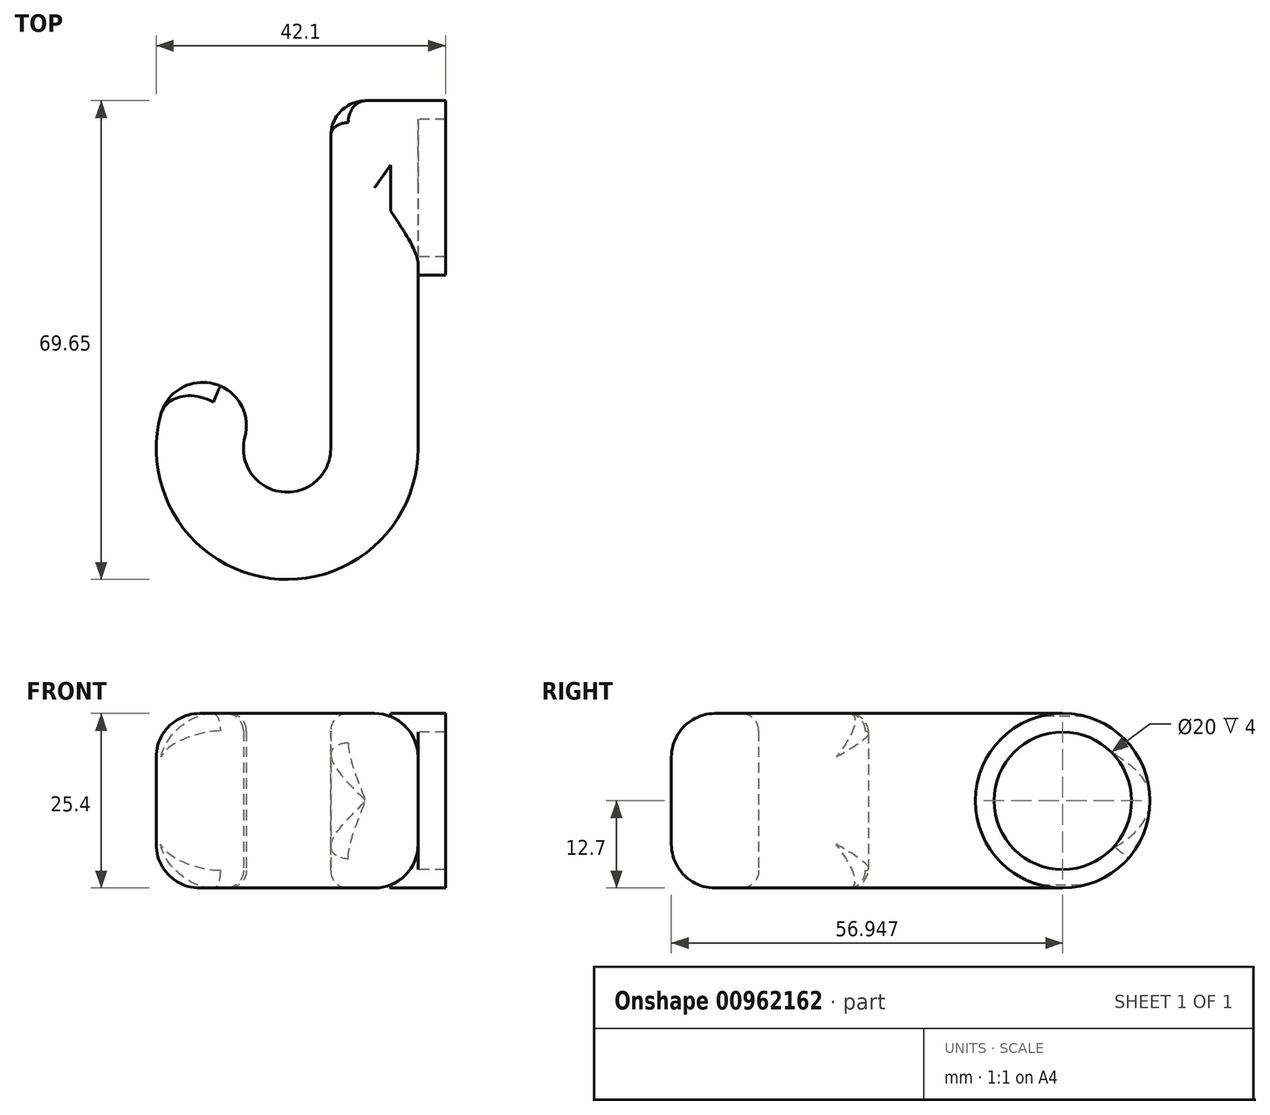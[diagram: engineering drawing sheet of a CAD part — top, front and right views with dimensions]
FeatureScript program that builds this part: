
annotation { "Feature Type Name" : "Feature", "Feature Type Description" : "" }
export const myFeature = defineFeature(function(context is Context, id is Id, definition is map)
    precondition{}
    {
        {
            var Q0;
            Q0=qCreatedBy(makeId("Top.planeOp"),FACE);
            var sketch = newSketch(context, id + "F0", { "sketchPlane" : qUnion([Q0])});
            skLineSegment(sketch, "E0", {"start": v(0, 38.1) * mm, "end": v(0, 12.7) * mm});
            skArc(sketch, "E1", {"start": v(10.84, 33.6) * mm, "mid": v(8.78, 43.97) * mm, "end": v(0, 38.1) * mm});
            skArc(sketch, "E2.0", {"start": v(19.82, 24.63) * mm, "mid": v(13.64, 55.7) * mm, "end": v(-12.7, 38.1) * mm});
            skLineSegment(sketch, "E3", {"start": v(10.84, 33.6) * mm, "end": v(19.82, 24.63) * mm});
            skArc(sketch, "E4", {"start": v(-23.54, 17.2) * mm, "mid": v(-21.48, 6.83) * mm, "end": v(-12.7, 12.7) * mm});
            skArc(sketch, "E5.0", {"start": v(-32.52, 26.17) * mm, "mid": v(-26.34, -4.9) * mm, "end": v(0, 12.7) * mm});
            skPoint(sketch, "E6.end.orphan", {"position": v(-19.05, 0) * mm});
            skPoint(sketch, "E7.orphan", {"position": v(-12.7, 12.7) * mm});
            skLineSegment(sketch, "E8", {"start": v(-23.54, 17.2) * mm, "end": v(-32.52, 26.17) * mm});
            skLineSegment(sketch, "E9", {"start": v(-12.7, 38.1) * mm, "end": v(-12.7, 12.7) * mm});
            skSolve(sketch);
        }
        {
            var Q0;
            Q0=qSketchRegion(id+"F0",true);
            extrude(context, id + "F1", {"entities" : qUnion([Q0]), "depth" : 76.2 * mm, "offsetDistance" : 25.4 * mm});
        }
        {
            var Q0;
            Q0=makeQuery(id+"F1.opExtrude","SWEPT_FACE",FACE,{"disambiguationData":[OSD([sQuery(id+"F0.wireOp",EDGE,"E9")])]});
            var sketch = newSketch(context, id + "F2", { "sketchPlane" : qUnion([Q0])});
            skLineSegment(sketch, "E10", {"start": v(0, 0) * mm, "end": v(-38.1, 0) * mm});
            skLineSegment(sketch, "E11", {"start": v(0, 76.2) * mm, "end": v(-38.1, 76.2) * mm});
            skLineSegment(sketch, "E12.bottom", {"start": v(-38.1, 0) * mm, "end": v(-25.4, 0) * mm});
            skLineSegment(sketch, "E12.top", {"start": v(-38.1, 76.2) * mm, "end": v(-25.4, 76.2) * mm});
            skLineSegment(sketch, "E12.right", {"start": v(-25.4, 0) * mm, "end": v(-25.4, 25.4) * mm});
            skLineSegment(sketch, "E13", {"start": v(-38.1, 50.8) * mm, "end": v(-57.15, 50.8) * mm});
            skLineSegment(sketch, "E14.MirrorCS", {"start": v(-38.1, 25.4) * mm, "end": v(-57.15, 25.4) * mm});
            skLineSegment(sketch, "E15", {"start": v(-57.15, 25.4) * mm, "end": v(-57.15, 50.8) * mm});
            skLineSegment(sketch, "E16.bottom", {"start": v(-25.4, 0) * mm, "end": v(6.35, 0) * mm});
            skLineSegment(sketch, "E16.top", {"start": v(-25.4, 25.4) * mm, "end": v(6.35, 25.4) * mm});
            skLineSegment(sketch, "E16.right", {"start": v(6.35, 0) * mm, "end": v(6.35, 25.4) * mm});
            skLineSegment(sketch, "E17", {"start": v(-25.4, 50.8) * mm, "end": v(6.35, 50.8) * mm});
            skLineSegment(sketch, "E18", {"start": v(6.35, 50.8) * mm, "end": v(6.35, 76.2) * mm});
            skLineSegment(sketch, "E19", {"start": v(6.35, 76.2) * mm, "end": v(-25.4, 76.2) * mm});
            skPoint(sketch, "E20.end.orphan", {"position": v(-25.4, 38.1) * mm});
            skPoint(sketch, "E20.start.orphan", {"position": v(-38.1, 38.1) * mm});
            skLineSegment(sketch, "E21", {"start": v(-38.1, 0) * mm, "end": v(-38.1, 76.2) * mm});
            skPoint(sketch, "E22.orphan", {"position": v(-25.4, 25.4) * mm});
            skLineSegment(sketch, "E23.trimOffspring", {"start": v(-25.4, 50.8) * mm, "end": v(-25.4, 76.2) * mm});
            skSolve(sketch);
        }
        {
            var Q0;
            {var subQ0=sQuery(id+"F2.wireOp",EDGE,"E13");Q0=makeQuery(id+"F2.imprint","IMPRINT",FACE,{"disambiguationData":[TD([[makeQuery(id+"F2.imprint","IMPRINT",EDGE,{"derivedFrom":subQ0}),1.0]])]});}
            extrude(context, id + "F3", {"entities" : qUnion([Q0]), "operationType" : NewBodyOperationType.REMOVE, "endBound" : BoundingType.THROUGH_ALL, "oppositeDirection" : true, "depth" : 25.4 * mm, "offsetDistance" : 25.4 * mm});
        }
        {
            var Q0;
            Q0=qSketchRegion(id+"F2",true);
            extrude(context, id + "F4", {"entities" : qUnion([Q0]), "operationType" : NewBodyOperationType.REMOVE, "oppositeDirection" : true, "depth" : 25.4 * mm, "offsetDistance" : 25.4 * mm});
        }
        {
            var Q0;
            Q0=makeQuery(id+"F3.boolean.opBoolean","COPY",FACE,{"disambiguationData":[TD([makeQuery(id+"F1.opExtrude","SWEPT_FACE",FACE,{"disambiguationData":[OSD([sQuery(id+"F0.wireOp",EDGE,"E1")])]}),makeQuery(id+"F1.opExtrude","SWEPT_FACE",FACE,{"disambiguationData":[OSD([sQuery(id+"F0.wireOp",EDGE,"E2.0")])]}),makeQuery(id+"F3.opExtrude","SWEPT_FACE",FACE,{"disambiguationData":[OSD([sQuery(id+"F2.wireOp",EDGE,"E13")])]}),makeQuery(id+"F3.opExtrude","SWEPT_FACE",FACE,{"disambiguationData":[OSD([sQuery(id+"F2.wireOp",EDGE,"E14.MirrorCS")])]})])],"derivedFrom":makeQuery(id+"F3.opExtrude","SWEPT_FACE",FACE,{"disambiguationData":[OSD([sQuery(id+"F2.wireOp",EDGE,"E21")])]})});
            var sketch = newSketch(context, id + "F5", { "sketchPlane" : qUnion([Q0])});
            skLineSegment(sketch, "E24.bottom", {"start": v(-25.4, 50.8) * mm, "end": v(-9.42, 50.8) * mm});
            skLineSegment(sketch, "E24.top", {"start": v(-25.4, 25.4) * mm, "end": v(-9.42, 25.4) * mm});
            skLineSegment(sketch, "E24.left", {"start": v(-25.4, 50.8) * mm, "end": v(-25.4, 25.4) * mm});
            skLineSegment(sketch, "E24.right", {"start": v(-9.42, 50.8) * mm, "end": v(-9.42, 25.4) * mm});
            skSolve(sketch);
        }
        {
            var Q0;
            Q0=qSketchRegion(id+"F5",true);
            extrude(context, id + "F6", {"entities" : qUnion([Q0]), "operationType" : NewBodyOperationType.REMOVE, "endBound" : BoundingType.THROUGH_ALL, "oppositeDirection" : true, "depth" : 25.4 * mm, "offsetDistance" : 25.4 * mm});
        }
        {
            var Q0;
            Q0=makeQuery(id+"F4.boolean.opBoolean","COPY",FACE,{"derivedFrom":makeQuery(id+"F4.opExtrude","CAP_FACE",FACE,{"disambiguationData":[OSD([sQuery(id+"F2.wireOp",EDGE,"E17"),sQuery(id+"F2.wireOp",EDGE,"E18"),sQuery(id+"F2.wireOp",EDGE,"E19"),sQuery(id+"F2.wireOp",EDGE,"E23.trimOffspring")])],"isStart":true})});
            var sketch = newSketch(context, id + "F7", { "sketchPlane" : qUnion([Q0])});
            skLineSegment(sketch, "E25.bottom", {"start": v(17.29, 76.2) * mm, "end": v(-6.4, 76.2) * mm});
            skLineSegment(sketch, "E25.top", {"start": v(17.29, 50.8) * mm, "end": v(-6.4, 50.8) * mm});
            skLineSegment(sketch, "E25.left", {"start": v(17.29, 76.2) * mm, "end": v(17.29, 50.8) * mm});
            skLineSegment(sketch, "E25.right", {"start": v(-6.4, 76.2) * mm, "end": v(-6.4, 50.8) * mm});
            skLineSegment(sketch, "E26.MirrorCS", {"start": v(17.29, 0) * mm, "end": v(17.29, 25.4) * mm});
            skLineSegment(sketch, "E27.MirrorCS", {"start": v(17.29, 25.4) * mm, "end": v(-6.4, 25.4) * mm});
            skLineSegment(sketch, "E28.MirrorCS", {"start": v(-6.4, 0) * mm, "end": v(-6.4, 25.4) * mm});
            skLineSegment(sketch, "E29.MirrorCS", {"start": v(17.29, 0) * mm, "end": v(-6.4, 0) * mm});
            skSolve(sketch);
        }
        {
            var Q0;
            Q0=qSketchRegion(id+"F7",true);
            extrude(context, id + "F8", {"entities" : qUnion([Q0]), "operationType" : NewBodyOperationType.REMOVE, "endBound" : BoundingType.THROUGH_ALL, "oppositeDirection" : true, "depth" : 25.4 * mm, "offsetDistance" : 25.4 * mm});
        }
        {
            var Q0;
            Q0=makeQuery(id+"F8.boolean.opBoolean","COPY",FACE,{"derivedFrom":makeQuery(id+"F8.opExtrude","SWEPT_FACE",FACE,{"disambiguationData":[OSD([sQuery(id+"F7.wireOp",EDGE,"E25.left")])]})});
            var sketch = newSketch(context, id + "F9", { "sketchPlane" : qUnion([Q0])});
            skLineSegment(sketch, "E30", {"start": v(-37.54, 76.2) * mm, "end": v(-37.54, 50.8) * mm});
            skLineSegment(sketch, "E31", {"start": v(-37.54, 50.8) * mm, "end": v(-23.64, 50.8) * mm});
            skLineSegment(sketch, "E32", {"start": v(-23.64, 50.8) * mm, "end": v(-23.64, 76.2) * mm});
            skLineSegment(sketch, "E33", {"start": v(-23.64, 76.2) * mm, "end": v(-37.54, 76.2) * mm});
            skLineSegment(sketch, "E34.MirrorCS", {"start": v(-37.54, 25.4) * mm, "end": v(-23.64, 25.4) * mm});
            skLineSegment(sketch, "E35.MirrorCS", {"start": v(-37.54, 0) * mm, "end": v(-37.54, 25.4) * mm});
            skLineSegment(sketch, "E36.MirrorCS", {"start": v(-23.64, 25.4) * mm, "end": v(-23.64, 0) * mm});
            skLineSegment(sketch, "E37.MirrorCS", {"start": v(-23.64, 0) * mm, "end": v(-37.54, 0) * mm});
            skSolve(sketch);
        }
        {
            var Q0;
            Q0=qSketchRegion(id+"F9",true);
            extrude(context, id + "F10", {"entities" : qUnion([Q0]), "operationType" : NewBodyOperationType.REMOVE, "endBound" : BoundingType.THROUGH_ALL, "oppositeDirection" : true, "depth" : 25.4 * mm, "offsetDistance" : 25.4 * mm});
        }
        {
            var Q0;
            Q0=makeQuery(id+"F4.boolean.opBoolean","INTERSECT",EDGE,{"derivedFrom":[makeQuery(id+"F1.opExtrude","SWEPT_FACE",FACE,{"disambiguationData":[OSD([sQuery(id+"F0.wireOp",EDGE,"E0")])]}),makeQuery(id+"F4.opExtrude","SWEPT_FACE",FACE,{"disambiguationData":[OSD([sQuery(id+"F2.wireOp",EDGE,"E12.right")])]})]});
            var Q1;
            Q1=makeQuery(id+"F4.boolean.opBoolean","COPY",EDGE,{"derivedFrom":makeQuery(id+"F4.opExtrude","CAP_EDGE",EDGE,{"disambiguationData":[OSD([sQuery(id+"F2.wireOp",EDGE,"E12.right")])],"isStart":true})});
            var Q2;
            Q2=makeQuery(id+"F4.boolean.opBoolean","INTERSECT",EDGE,{"derivedFrom":[makeQuery(id+"F1.opExtrude","SWEPT_FACE",FACE,{"disambiguationData":[OSD([sQuery(id+"F0.wireOp",EDGE,"E0")])]}),makeQuery(id+"F4.opExtrude","SWEPT_FACE",FACE,{"disambiguationData":[OSD([sQuery(id+"F2.wireOp",EDGE,"E23.trimOffspring")])]})]});
            var Q3;
            Q3=makeQuery(id+"F4.boolean.opBoolean","COPY",EDGE,{"derivedFrom":makeQuery(id+"F4.opExtrude","CAP_EDGE",EDGE,{"disambiguationData":[OSD([sQuery(id+"F2.wireOp",EDGE,"E23.trimOffspring")])],"isStart":true})});
            var Q4;
            {var subQ0=sQuery(id+"F0.wireOp",EDGE,"E0");Q4=makeQuery(id+"F3.boolean.opBoolean","SPLIT",EDGE,{"disambiguationData":[topologyDisambiguationEdgeConnected([makeQuery(id+"F1.opExtrude","SWEPT_FACE",FACE,{"disambiguationData":[OSD([subQ0])]}),makeQuery(id+"F3.opExtrude","SWEPT_FACE",FACE,{"disambiguationData":[OSD([sQuery(id+"F2.wireOp",EDGE,"E21")])]})])],"derivedFrom":makeQuery(id+"F1.opExtrude","SWEPT_EDGE",EDGE,{"disambiguationData":[OSD([subQ0,sQuery(id+"F0.wireOp",EDGE,"E1")])]})});}
            var Q5;
            Q5=makeQuery(id+"F3.boolean.opBoolean","MERGE",EDGE,{"derivedFrom":[makeQuery(id+"F1.opExtrude","SWEPT_EDGE",EDGE,{"disambiguationData":[OSD([sQuery(id+"F0.wireOp",EDGE,"E2.0"),sQuery(id+"F0.wireOp",EDGE,"E9")])]})],"fromTools":[makeQuery(id+"F3.opExtrude","CAP_EDGE",EDGE,{"disambiguationData":[OSD([sQuery(id+"F2.wireOp",EDGE,"E21")])],"isStart":true})]});
            var Q6;
            {var subQ0=sQuery(id+"F0.wireOp",EDGE,"E3");var subQ1=sQuery(id+"F0.wireOp",EDGE,"E2.0");Q6=makeQuery(id+"F6.boolean.opBoolean","SPLIT",EDGE,{"disambiguationData":[TD([makeQuery(id+"F3.boolean.opBoolean","COPY",FACE,{"derivedFrom":makeQuery(id+"F3.opExtrude","SWEPT_FACE",FACE,{"disambiguationData":[OSD([sQuery(id+"F2.wireOp",EDGE,"E14.MirrorCS")])]})})])],"derivedFrom":makeQuery(id+"F1.opExtrude","SWEPT_EDGE",EDGE,{"disambiguationData":[OSD([subQ1,subQ0])]})});}
            var Q7;
            {var subQ0=sQuery(id+"F0.wireOp",EDGE,"E3");var subQ1=sQuery(id+"F0.wireOp",EDGE,"E1");Q7=makeQuery(id+"F6.boolean.opBoolean","SPLIT",EDGE,{"disambiguationData":[TD([makeQuery(id+"F3.boolean.opBoolean","COPY",FACE,{"derivedFrom":makeQuery(id+"F3.opExtrude","SWEPT_FACE",FACE,{"disambiguationData":[OSD([sQuery(id+"F2.wireOp",EDGE,"E14.MirrorCS")])]})})])],"derivedFrom":makeQuery(id+"F1.opExtrude","SWEPT_EDGE",EDGE,{"disambiguationData":[OSD([subQ1,subQ0])]})});}
            var Q8;
            {var subQ0=sQuery(id+"F0.wireOp",EDGE,"E3");var subQ1=sQuery(id+"F0.wireOp",EDGE,"E2.0");Q8=makeQuery(id+"F6.boolean.opBoolean","SPLIT",EDGE,{"disambiguationData":[TD([makeQuery(id+"F3.boolean.opBoolean","COPY",FACE,{"derivedFrom":makeQuery(id+"F3.opExtrude","SWEPT_FACE",FACE,{"disambiguationData":[OSD([sQuery(id+"F2.wireOp",EDGE,"E13")])]})})])],"derivedFrom":makeQuery(id+"F1.opExtrude","SWEPT_EDGE",EDGE,{"disambiguationData":[OSD([subQ1,subQ0])]})});}
            var Q9;
            {var subQ0=sQuery(id+"F0.wireOp",EDGE,"E3");var subQ1=sQuery(id+"F0.wireOp",EDGE,"E1");Q9=makeQuery(id+"F6.boolean.opBoolean","SPLIT",EDGE,{"disambiguationData":[TD([makeQuery(id+"F3.boolean.opBoolean","COPY",FACE,{"derivedFrom":makeQuery(id+"F3.opExtrude","SWEPT_FACE",FACE,{"disambiguationData":[OSD([sQuery(id+"F2.wireOp",EDGE,"E13")])]})})])],"derivedFrom":makeQuery(id+"F1.opExtrude","SWEPT_EDGE",EDGE,{"disambiguationData":[OSD([subQ1,subQ0])]})});}
            var Q10;
            Q10=makeQuery(id+"F1.opExtrude","SWEPT_EDGE",EDGE,{"disambiguationData":[OSD([sQuery(id+"F0.wireOp",EDGE,"E5.0"),sQuery(id+"F0.wireOp",EDGE,"E8")])]});
            var Q11;
            Q11=makeQuery(id+"F1.opExtrude","SWEPT_EDGE",EDGE,{"disambiguationData":[OSD([sQuery(id+"F0.wireOp",EDGE,"E4"),sQuery(id+"F0.wireOp",EDGE,"E8")])]});
            var Q12;
            Q12=makeQuery(id+"F10.boolean.opBoolean","INTERSECT",EDGE,{"derivedFrom":[makeQuery(id+"F1.opExtrude","SWEPT_FACE",FACE,{"disambiguationData":[OSD([sQuery(id+"F0.wireOp",EDGE,"E5.0")])]}),makeQuery(id+"F10.opExtrude","SWEPT_FACE",FACE,{"disambiguationData":[OSD([sQuery(id+"F9.wireOp",EDGE,"E31")])]})]});
            var Q13;
            Q13=makeQuery(id+"F10.boolean.opBoolean","INTERSECT",EDGE,{"derivedFrom":[makeQuery(id+"F1.opExtrude","SWEPT_FACE",FACE,{"disambiguationData":[OSD([sQuery(id+"F0.wireOp",EDGE,"E5.0")])]}),makeQuery(id+"F10.opExtrude","SWEPT_FACE",FACE,{"disambiguationData":[OSD([sQuery(id+"F9.wireOp",EDGE,"E34.MirrorCS")])]})]});
            var Q14;
            Q14=makeQuery(id+"F1.opExtrude","CAP_EDGE",EDGE,{"disambiguationData":[OSD([sQuery(id+"F0.wireOp",EDGE,"E2.0")])],"isStart":true});
            var Q15;
            Q15=makeQuery(id+"F6.boolean.opBoolean","INTERSECT",EDGE,{"derivedFrom":[makeQuery(id+"F1.opExtrude","SWEPT_FACE",FACE,{"disambiguationData":[OSD([sQuery(id+"F0.wireOp",EDGE,"E2.0")])]}),makeQuery(id+"F6.opExtrude","SWEPT_FACE",FACE,{"disambiguationData":[OSD([sQuery(id+"F5.wireOp",EDGE,"E24.top")])]})]});
            var Q16;
            Q16=makeQuery(id+"F1.opExtrude","CAP_EDGE",EDGE,{"disambiguationData":[OSD([sQuery(id+"F0.wireOp",EDGE,"E2.0")])],"isStart":false});
            var Q17;
            Q17=makeQuery(id+"F6.boolean.opBoolean","INTERSECT",EDGE,{"derivedFrom":[makeQuery(id+"F1.opExtrude","SWEPT_FACE",FACE,{"disambiguationData":[OSD([sQuery(id+"F0.wireOp",EDGE,"E2.0")])]}),makeQuery(id+"F6.opExtrude","SWEPT_FACE",FACE,{"disambiguationData":[OSD([sQuery(id+"F5.wireOp",EDGE,"E24.bottom")])]})]});
            fillet(context, id + "F11", {"entities" : qUnion([Q0, Q1, Q2, Q3, Q4, Q5, Q6, Q7, Q8, Q9, Q10, Q11, Q12, Q13, Q14, Q15, Q16, Q17]), "radius" : 6.35 * mm, "tangentPropagation" : true, "allowEdgeOverflow" : false});
        }
        {
            var Q0;
            Q0=qCreatedBy(makeId("Top.planeOp"),FACE);
            var sketch = newSketch(context, id + "F12", { "sketchPlane" : qUnion([Q0])});
            skLineSegment(sketch, "E38.bottom", {"start": v(-21.45, 59.3) * mm, "end": v(30.69, 59.3) * mm});
            skLineSegment(sketch, "E38.top", {"start": v(-21.45, 25.2) * mm, "end": v(30.69, 25.2) * mm});
            skLineSegment(sketch, "E38.left", {"start": v(-21.45, 59.3) * mm, "end": v(-21.45, 25.2) * mm});
            skLineSegment(sketch, "E38.right", {"start": v(30.69, 59.3) * mm, "end": v(30.69, 25.2) * mm});
            skSolve(sketch);
        }
        {
            var Q0;
            Q0 = qSketchRegion(id + "F12", true);
            var Q1;
            {var subQ0=sQuery(id+"F0.wireOp",EDGE,"E2.0");var subQ1=sQuery(id+"F0.wireOp",EDGE,"E1");var subQ2=sQuery(id+"F0.wireOp",EDGE,"E3");var subQ3=sQuery(id+"F0.wireOp",EDGE,"E0");var subQ4=sQuery(id+"F0.wireOp",EDGE,"E9");Q1=makeQuery(id+"F4.boolean.opBoolean","SPLIT",FACE,{"disambiguationData":[TD([makeQuery(id+"F1.opExtrude","SWEPT_FACE",FACE,{"disambiguationData":[OSD([subQ3])]})])],"derivedFrom":makeQuery(id+"F1.opExtrude","CAP_FACE",FACE,{"disambiguationData":[OSD([subQ3,subQ1,subQ0,subQ2,sQuery(id+"F0.wireOp",EDGE,"E4"),sQuery(id+"F0.wireOp",EDGE,"E5.0"),sQuery(id+"F0.wireOp",EDGE,"E8"),subQ4])],"isStart":false})});}
            extrude(context, id + "F13", {"entities" : qUnion([Q0]), "operationType" : NewBodyOperationType.REMOVE, "endBound" : BoundingType.UP_TO_SURFACE, "depth" : 25.4 * mm, "endBoundEntityFace" : qUnion([Q1]), "offsetDistance" : 25.4 * mm});
        }
        {
            var Q0;
            Q0=makeQuery(id+"F1.opExtrude","SWEPT_FACE",FACE,{"disambiguationData":[OSD([sQuery(id+"F0.wireOp",EDGE,"E0")])]});
            var sketch = newSketch(context, id + "F14", { "sketchPlane" : qUnion([Q0])});
            skCircle(sketch, "E39", {"center": v(50.6, 38.1) * mm, "radius": 10 * mm});
            skCircle(sketch, "E40", {"center": v(50.6, 38.1) * mm, "radius": 12.7 * mm});
            skSolve(sketch);
        }
        {
            var Q0;
            Q0=makeQuery(id+"F13.boolean.opBoolean","COPY",FACE,{"derivedFrom":makeQuery(id+"F13.opExtrude","SWEPT_FACE",FACE,{"disambiguationData":[OSD([sQuery(id+"F12.wireOp",EDGE,"E38.top")])]})});
            extrude(context, id + "F15", {"entities" : qUnion([Q0]), "operationType" : NewBodyOperationType.ADD, "depth" : 38.1 * mm, "offsetDistance" : 25.4 * mm});
        }
        {
            var Q0;
            Q0=makeQuery(id+"F14.imprint","IMPRINT",FACE,{"disambiguationData":[TD([[makeQuery(id+"F14.imprint","IMPRINT",EDGE,{"derivedFrom":sQuery(id+"F14.wireOp",EDGE,"E39")}),-1.0]])]});
            extrude(context, id + "F16", {"entities" : qUnion([Q0]), "operationType" : NewBodyOperationType.ADD, "endBound" : BoundingType.SYMMETRIC, "depth" : 8 * mm, "offsetDistance" : 25.4 * mm});
        }
        {
            var Q0;
            Q0=makeQuery(id+"F15.opExtrude","CAP_EDGE",EDGE,{"disambiguationData":[OSD([sQuery(id+"F0.wireOp",EDGE,"E9"),sQuery(id+"F12.wireOp",EDGE,"E38.top")])],"isStart":false});
            fillet(context, id + "F17", {"entities" : qUnion([Q0]), "radius" : 5.08 * mm, "tangentPropagation" : true, "allowEdgeOverflow" : false});
        }
        {
            var Q0;
            Q0=makeQuery(id+"F16.opExtrude","CAP_FACE",FACE,{"disambiguationData":[OSD([sQuery(id+"F14.wireOp",EDGE,"E39"),sQuery(id+"F14.wireOp",EDGE,"E40")])],"isStart":false});
            var sketch = newSketch(context, id + "F18", { "sketchPlane" : qUnion([Q0])});
            skCircle(sketch, "E41", {"center": v(50.6, 38.1) * mm, "radius": 12.7 * mm});
            skLineSegment(sketch, "E42", {"start": v(50.6, 50.8) * mm, "end": v(63.36, 50.8) * mm});
            skLineSegment(sketch, "E43", {"start": v(63.36, 50.8) * mm, "end": v(63.36, 38.1) * mm});
            skLineSegment(sketch, "E44", {"start": v(63.36, 38.1) * mm, "end": v(63.3, 38.1) * mm});
            skLineSegment(sketch, "E45.MirrorCS", {"start": v(63.36, 25.4) * mm, "end": v(63.36, 38.1) * mm});
            skLineSegment(sketch, "E46.MirrorCS", {"start": v(50.6, 25.4) * mm, "end": v(63.36, 25.4) * mm});
            skSolve(sketch);
        }
        {
            var Q0;
            {var subQ0=sQuery(id+"F18.wireOp",EDGE,"E42");Q0=makeQuery(id+"F18.imprint","IMPRINT",FACE,{"disambiguationData":[TD([[makeQuery(id+"F18.imprint","IMPRINT",EDGE,{"derivedFrom":subQ0}),-1.0]])]});}
            var Q1;
            {var subQ0=sQuery(id+"F18.wireOp",EDGE,"E44");Q1=makeQuery(id+"F18.imprint","IMPRINT",FACE,{"disambiguationData":[TD([[makeQuery(id+"F18.imprint","IMPRINT",EDGE,{"derivedFrom":subQ0}),1.0]])]});}
            var Q2;
            {var subQ0=sQuery(id+"F0.wireOp",EDGE,"E9");Q2=makeQuery(id+"F15.boolean.opBoolean","MERGE",FACE,{"derivedFrom":[makeQuery(id+"F1.opExtrude","SWEPT_FACE",FACE,{"disambiguationData":[OSD([subQ0])]}),makeQuery(id+"F15.opExtrude","SWEPT_FACE",FACE,{"disambiguationData":[OSD([subQ0,sQuery(id+"F12.wireOp",EDGE,"E38.top")])]})]});}
            extrude(context, id + "F19", {"entities" : qUnion([Q0, Q1]), "operationType" : NewBodyOperationType.REMOVE, "endBound" : BoundingType.UP_TO_SURFACE, "oppositeDirection" : true, "depth" : 25.4 * mm, "endBoundEntityFace" : qUnion([Q2]), "offsetDistance" : 25.4 * mm});
        }
        {
            var Q0;
            {var subQ0=sQuery(id+"F12.wireOp",EDGE,"E38.top");var subQ1=sQuery(id+"F2.wireOp",EDGE,"E17");var subQ2=sQuery(id+"F0.wireOp",EDGE,"E0");var subQ3=sQuery(id+"F2.wireOp",EDGE,"E16.top");Q0=makeQuery(id+"F16.boolean.opBoolean","SPLIT",FACE,{"disambiguationData":[TD([makeQuery(id+"F11.opFillet","BLEND_FACE",FACE,{"disambiguationData":[OSD([subQ2,subQ3])]}),makeQuery(id+"F11.opFillet","BLEND_FACE",FACE,{"disambiguationData":[OSD([subQ2,subQ1])]}),makeQuery(id+"F15.opExtrude","SWEPT_FACE",FACE,{"disambiguationData":[OSD([subQ2,subQ3,subQ0])]}),makeQuery(id+"F15.opExtrude","SWEPT_FACE",FACE,{"disambiguationData":[OSD([subQ2,subQ1,subQ0])]}),makeQuery(id+"F16.opExtrude","SWEPT_FACE",FACE,{"disambiguationData":[OSD([sQuery(id+"F14.wireOp",EDGE,"E39")])]})])],"derivedFrom":makeQuery(id+"F15.boolean.opBoolean","MERGE",FACE,{"derivedFrom":[makeQuery(id+"F1.opExtrude","SWEPT_FACE",FACE,{"disambiguationData":[OSD([subQ2])]}),makeQuery(id+"F15.opExtrude","SWEPT_FACE",FACE,{"disambiguationData":[OSD([subQ2,subQ0])]})]})});}
            var sketch = newSketch(context, id + "F20", { "sketchPlane" : qUnion([Q0])});
            skCircle(sketch, "E47", {"center": v(50.6, 38.1) * mm, "radius": 10 * mm});
            skSolve(sketch);
        }
        {
            var Q0;
            Q0 = qSketchRegion(id + "F20", true);
            var Q1;
            {var subQ0=sQuery(id+"F0.wireOp",EDGE,"E9");Q1=makeQuery(id+"F15.boolean.opBoolean","MERGE",FACE,{"derivedFrom":[makeQuery(id+"F1.opExtrude","SWEPT_FACE",FACE,{"disambiguationData":[OSD([subQ0])]}),makeQuery(id+"F15.opExtrude","SWEPT_FACE",FACE,{"disambiguationData":[OSD([subQ0,sQuery(id+"F12.wireOp",EDGE,"E38.top")])]})]});}
            extrude(context, id + "F21", {"entities" : qUnion([Q0]), "operationType" : NewBodyOperationType.ADD, "oppositeDirection" : true, "depth" : 10.16 * mm, "endBoundEntityFace" : qUnion([Q1]), "offsetDistance" : 25.4 * mm});
        }
        {
            var Q0;
            {var subQ0=makeQuery(id+"F1.opExtrude","SWEPT_FACE",FACE,{"disambiguationData":[OSD([sQuery(id+"F0.wireOp",EDGE,"E5.0")])]});Q0=makeQuery(id+"F11.opFillet","BLEND_EDGE",EDGE,{"blendedFrom":[makeQuery(id+"F10.boolean.opBoolean","INTERSECT",EDGE,{"derivedFrom":[subQ0,makeQuery(id+"F10.opExtrude","SWEPT_FACE",FACE,{"disambiguationData":[OSD([sQuery(id+"F9.wireOp",EDGE,"E34.MirrorCS")])]})]}),subQ0],"blendedInto":[subQ0]});}
            var Q1;
            {var subQ0=makeQuery(id+"F1.opExtrude","SWEPT_FACE",FACE,{"disambiguationData":[OSD([sQuery(id+"F0.wireOp",EDGE,"E5.0")])]});Q1=makeQuery(id+"F11.opFillet","BLEND_EDGE",EDGE,{"blendedFrom":[makeQuery(id+"F10.boolean.opBoolean","INTERSECT",EDGE,{"derivedFrom":[subQ0,makeQuery(id+"F10.opExtrude","SWEPT_FACE",FACE,{"disambiguationData":[OSD([sQuery(id+"F9.wireOp",EDGE,"E31")])]})]}),subQ0],"blendedInto":[subQ0]});}
            var Q2;
            Q2=makeQuery(id+"F8.boolean.opBoolean","INTERSECT",EDGE,{"derivedFrom":[makeQuery(id+"F1.opExtrude","SWEPT_FACE",FACE,{"disambiguationData":[OSD([sQuery(id+"F0.wireOp",EDGE,"E4")])]}),makeQuery(id+"F8.opExtrude","SWEPT_FACE",FACE,{"disambiguationData":[OSD([sQuery(id+"F7.wireOp",EDGE,"E25.top")])]})]});
            var Q3;
            Q3=makeQuery(id+"F8.boolean.opBoolean","INTERSECT",EDGE,{"derivedFrom":[makeQuery(id+"F1.opExtrude","SWEPT_FACE",FACE,{"disambiguationData":[OSD([sQuery(id+"F0.wireOp",EDGE,"E4")])]}),makeQuery(id+"F8.opExtrude","SWEPT_FACE",FACE,{"disambiguationData":[OSD([sQuery(id+"F7.wireOp",EDGE,"E27.MirrorCS")])]})]});
            fillet(context, id + "F22", {"entities" : qUnion([Q0, Q1, Q2, Q3]), "radius" : 2.54 * mm, "tangentPropagation" : true, "allowEdgeOverflow" : false});
        }
    });
